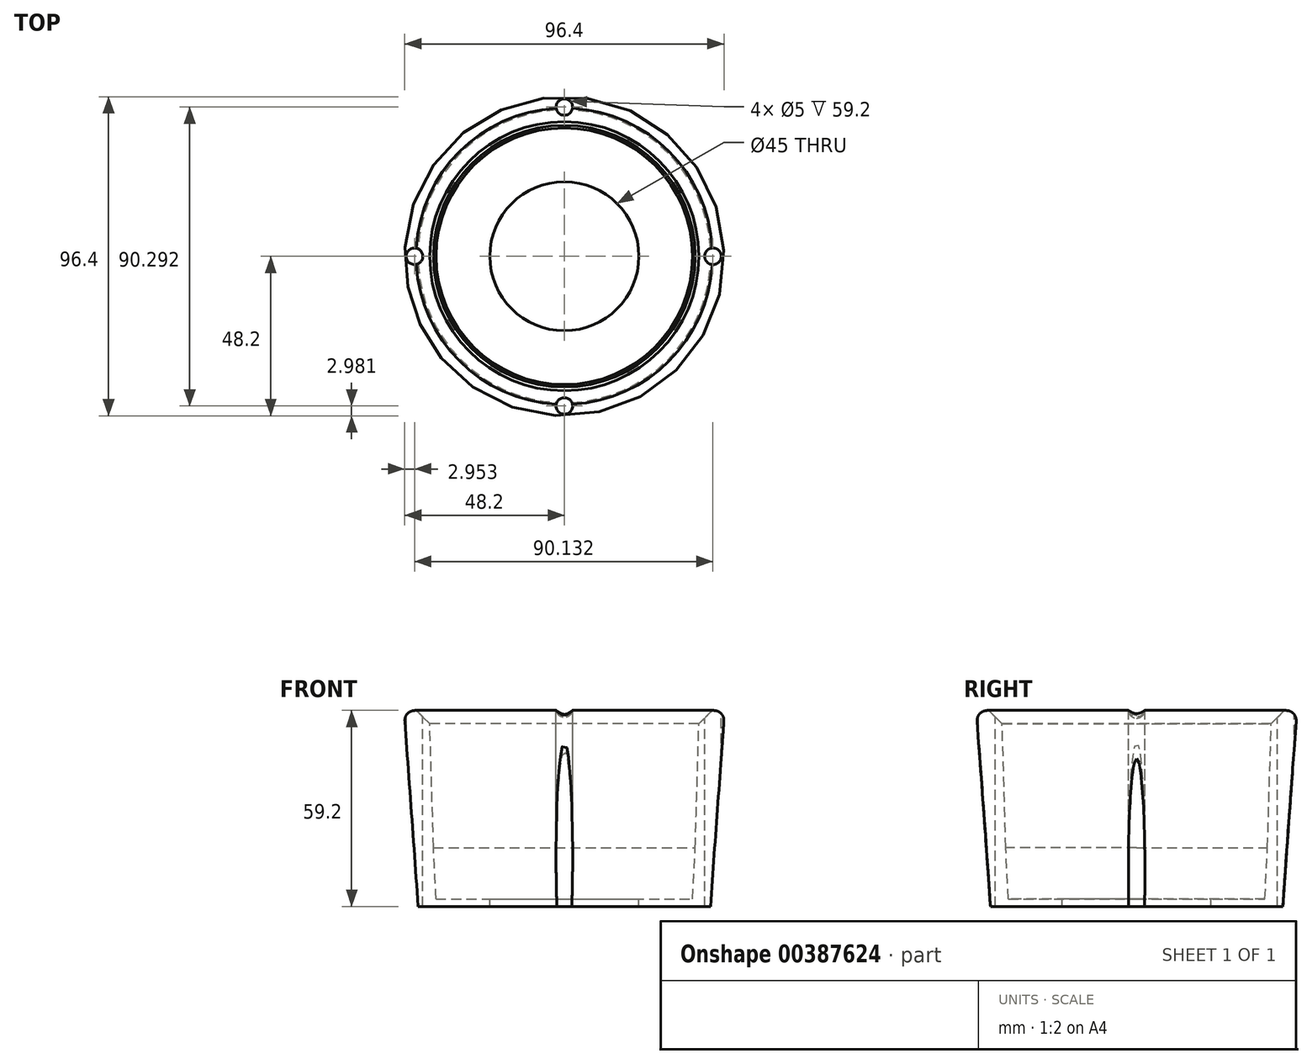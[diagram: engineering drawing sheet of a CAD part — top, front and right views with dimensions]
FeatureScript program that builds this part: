
annotation { "Feature Type Name" : "Feature", "Feature Type Description" : "" }
export const myFeature = defineFeature(function(context is Context, id is Id, definition is map)
    precondition{}
    {
        {
            var Q0;
            Q0=qCreatedBy(makeId("Front.planeOp"),FACE);
            var sketch = newSketch(context, id + "F0", { "sketchPlane" : qUnion([Q0])});
            skLineSegment(sketch, "E0.left", {"start": v(0, 0) * mm, "end": v(0, 2.27) * mm});
            skLineSegment(sketch, "E1", {"start": v(-44.22, 0) * mm, "end": v(-48.42, 59.2) * mm});
            skLineSegment(sketch, "E2", {"start": v(0, 2.27) * mm, "end": v(-38.75, 2.27) * mm});
            skLineSegment(sketch, "E3", {"start": v(-40.76, 59.2) * mm, "end": v(-39.53, 17.8) * mm});
            skLineSegment(sketch, "E4", {"start": v(-39.53, 17.8) * mm, "end": v(-38.75, 2.27) * mm});
            skLineSegment(sketch, "E5", {"start": v(-40.76, 59.2) * mm, "end": v(-48.42, 59.2) * mm});
            skLineSegment(sketch, "E6", {"start": v(0, 0) * mm, "end": v(-44.22, 0) * mm});
            skSolve(sketch);
        }
        {
            var Q0;
            Q0=makeQuery(id+"F0.imprint","IMPRINT",FACE,{"disambiguationData":[TD([[makeQuery(id+"F0.imprint","IMPRINT",EDGE,{"derivedFrom":sQuery(id+"F0.wireOp",EDGE,"E0.left")}),1.0]])]});
            var Q1;
            Q1=sQuery(id+"F0.wireOp",EDGE,"E0.left");
            revolve(context, id + "F1", {"entities" : qUnion([Q0]), "axis" : qUnion([Q1]), "revolveType" : RevolveType.FULL});
        }
        {
            var Q0;
            Q0=makeQuery(id+"F1.opRevolve","SWEPT_EDGE",EDGE,{"disambiguationData":[OSD([sQuery(id+"F0.wireOp",EDGE,"E1"),sQuery(id+"F0.wireOp",EDGE,"E5")])]});
            fillet(context, id + "F2", {"entities" : qUnion([Q0]), "radius" : 3 * mm, "tangentPropagation" : true, "allowEdgeOverflow" : false});
        }
        {
            var Q0;
            Q0=makeQuery(id+"F1.opRevolve","SWEPT_EDGE",EDGE,{"disambiguationData":[OSD([sQuery(id+"F0.wireOp",EDGE,"E3"),sQuery(id+"F0.wireOp",EDGE,"E5")])]});
            chamfer(context, id + "F3", {"entities" : qUnion([Q0]), "width" : 4 * mm, "tangentPropagation" : true});
        }
        {
            var Q0;
            Q0=qCreatedBy(makeId("Top.planeOp"),FACE);
            var sketch = newSketch(context, id + "F4", { "sketchPlane" : qUnion([Q0])});
            skPoint(sketch, "E7", {"position": v(0, 0) * mm});
            skPoint(sketch, "E8", {"position": v(-45.25, 0) * mm});
            skPoint(sketch, "E9", {"position": v(44.89, 0) * mm});
            skPoint(sketch, "E10", {"position": v(0, 45.07) * mm});
            skPoint(sketch, "E11", {"position": v(0, -45.22) * mm});
            skSolve(sketch);
        }
        {
            var Q0;
            Q0=sQuery(id+"F4.wireOp",VERTEX,"E7");
            var Q1;
            Q1=makeQuery(id+"F1.opRevolve","SWEPT_BODY",BODY,{"disambiguationData":[OSD([sQuery(id+"F0.wireOp",EDGE,"E0.left"),sQuery(id+"F0.wireOp",EDGE,"E1"),sQuery(id+"F0.wireOp",EDGE,"E2"),sQuery(id+"F0.wireOp",EDGE,"E3"),sQuery(id+"F0.wireOp",EDGE,"E4"),sQuery(id+"F0.wireOp",EDGE,"E5"),sQuery(id+"F0.wireOp",EDGE,"E6")])]});
            hole(context, id + "F5", {"style" : HoleStyle.SIMPLE, "endStyle" : HoleEndStyle.THROUGH, "oppositeDirection" : true, "holeDiameter" : 45 * mm, "isTappedThrough" : true, "tappedDepth" : 12 * mm, "tapClearance" : 3, "locations" : qUnion([Q0]), "scope" : qUnion([Q1]), "startStyle" : HoleStartStyle.SKETCH});
        }
        {
            var Q0;
            Q0=sQuery(id+"F4.wireOp",VERTEX,"E8");
            var Q1;
            Q1=sQuery(id+"F4.wireOp",VERTEX,"E10");
            var Q2;
            Q2=sQuery(id+"F4.wireOp",VERTEX,"E9");
            var Q3;
            Q3=sQuery(id+"F4.wireOp",VERTEX,"E11");
            var Q4;
            Q4=makeQuery(id+"F1.opRevolve","SWEPT_BODY",BODY,{"disambiguationData":[OSD([sQuery(id+"F0.wireOp",EDGE,"E0.left"),sQuery(id+"F0.wireOp",EDGE,"E1"),sQuery(id+"F0.wireOp",EDGE,"E2"),sQuery(id+"F0.wireOp",EDGE,"E3"),sQuery(id+"F0.wireOp",EDGE,"E4"),sQuery(id+"F0.wireOp",EDGE,"E5"),sQuery(id+"F0.wireOp",EDGE,"E6")])]});
            hole(context, id + "F6", {"style" : HoleStyle.SIMPLE, "endStyle" : HoleEndStyle.THROUGH, "oppositeDirection" : true, "holeDiameter" : 5 * mm, "isTappedThrough" : true, "tappedDepth" : 12 * mm, "tapClearance" : 3, "locations" : qUnion([Q0, Q1, Q2, Q3]), "scope" : qUnion([Q4]), "startStyle" : HoleStartStyle.SKETCH});
        }
    });
